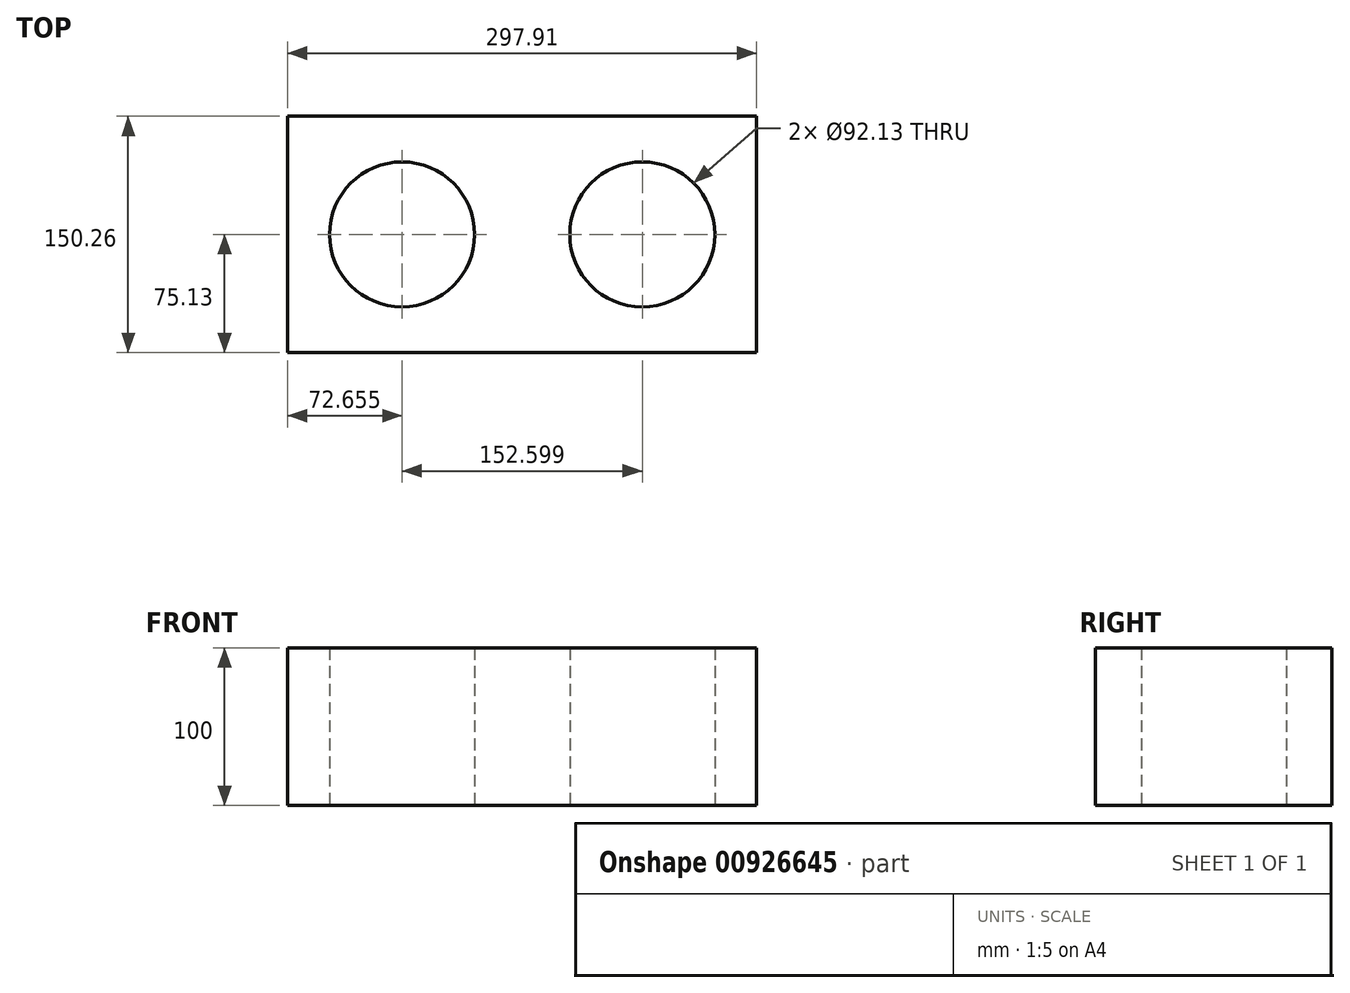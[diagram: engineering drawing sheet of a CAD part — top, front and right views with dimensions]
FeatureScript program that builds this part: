
annotation { "Feature Type Name" : "Feature", "Feature Type Description" : "" }
export const myFeature = defineFeature(function(context is Context, id is Id, definition is map)
    precondition{}
    {
        {
            var Q0;
            Q0=qCreatedBy(makeId("Top.planeOp"),FACE);
            var sketch = newSketch(context, id + "F0", { "sketchPlane" : qUnion([Q0])});
            skLineSegment(sketch, "E0.bottom", {"start": v(-74.48, 75.13) * mm, "end": v(74.48, 75.13) * mm});
            skLineSegment(sketch, "E0.top", {"start": v(-74.48, -75.13) * mm, "end": v(74.48, -75.13) * mm});
            skLineSegment(sketch, "E0.left", {"start": v(-74.48, 75.13) * mm, "end": v(-74.48, -75.13) * mm});
            skLineSegment(sketch, "E0.right", {"start": v(74.48, 75.13) * mm, "end": v(74.48, -75.13) * mm});
            skPoint(sketch, "E0.middle", {"position": v(0, 0) * mm});
            skCircle(sketch, "E1", {"center": v(1.82, 0) * mm, "radius": 46.07 * mm});
            skCircle(sketch, "E2.MirrorC", {"center": v(-150.78, 0) * mm, "radius": 46.07 * mm});
            skLineSegment(sketch, "E3.MirrorCS", {"start": v(-74.48, -75.13) * mm, "end": v(-223.43, -75.13) * mm});
            skLineSegment(sketch, "E4.MirrorCS", {"start": v(-223.43, 75.13) * mm, "end": v(-223.43, -75.13) * mm});
            skLineSegment(sketch, "E5.MirrorCS", {"start": v(-74.48, 75.13) * mm, "end": v(-223.43, 75.13) * mm});
            skLineSegment(sketch, "E6", {"start": v(-74.48, 75.13) * mm, "end": v(-74.48, 97.73) * mm});
            skSolve(sketch);
        }
        {
            var Q0;
            Q0=makeQuery(id+"F0.imprint","IMPRINT",FACE,{"disambiguationData":[TD([[makeQuery(id+"F0.imprint","IMPRINT",EDGE,{"derivedFrom":sQuery(id+"F0.wireOp",EDGE,"E0.bottom")}),-1.0]])]});
            var Q1;
            Q1=makeQuery(id+"F0.imprint","IMPRINT",FACE,{"disambiguationData":[TD([[makeQuery(id+"F0.imprint","IMPRINT",EDGE,{"derivedFrom":sQuery(id+"F0.wireOp",EDGE,"E0.left")}),-1.0]])]});
            extrude(context, id + "F1", {"entities" : qUnion([Q0, Q1]), "depth" : 100 * mm, "offsetDistance" : 25 * mm});
        }
    });
